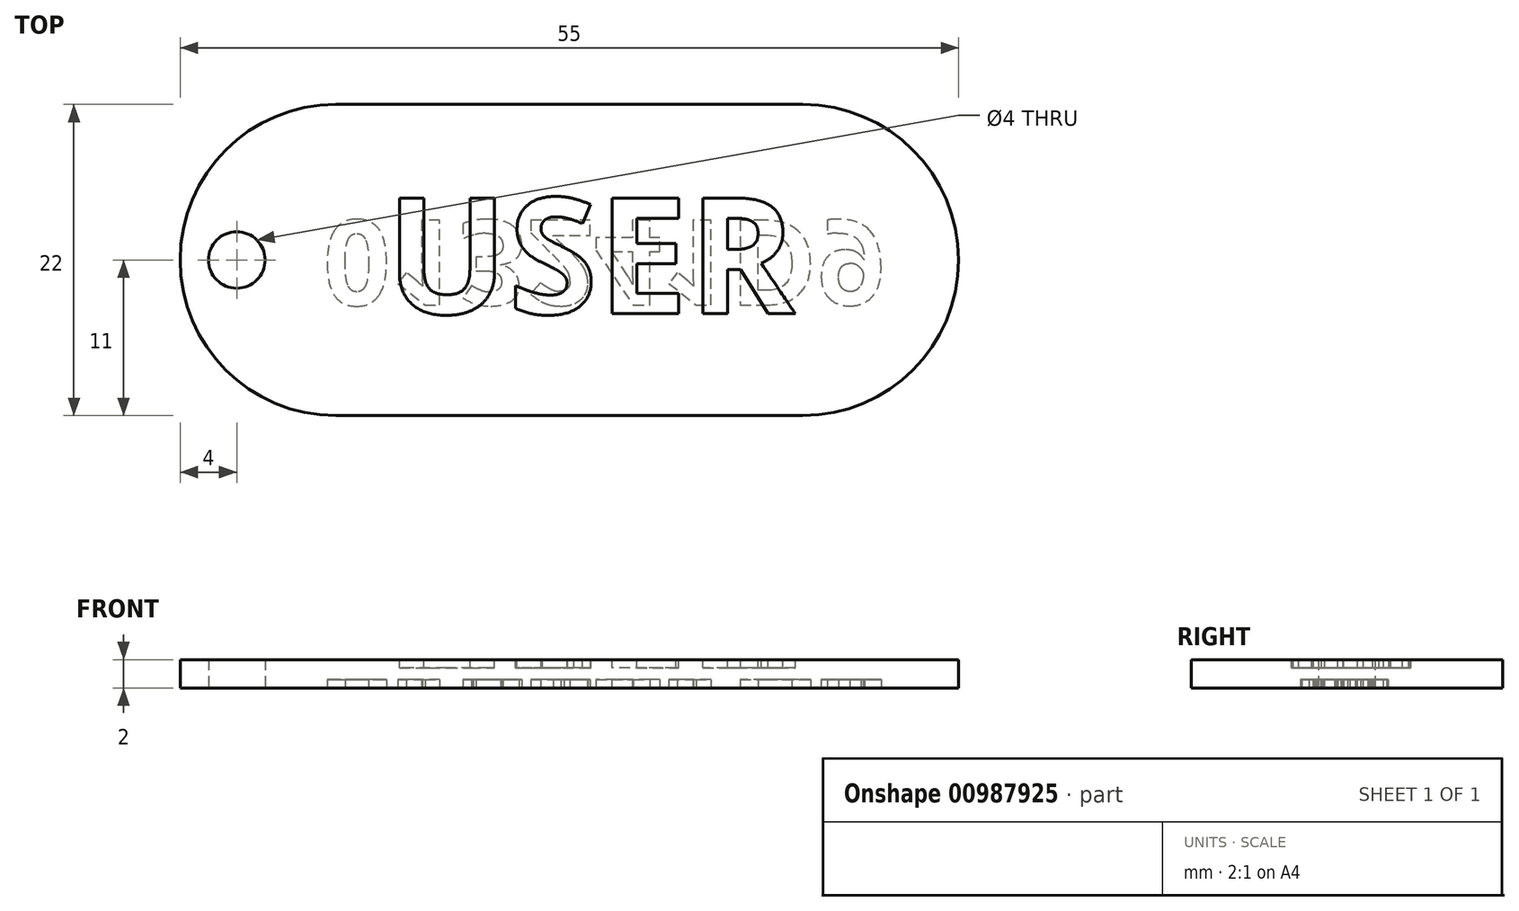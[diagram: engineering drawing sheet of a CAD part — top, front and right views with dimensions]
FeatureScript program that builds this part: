
annotation { "Feature Type Name" : "Feature", "Feature Type Description" : "" }
export const myFeature = defineFeature(function(context is Context, id is Id, definition is map)
    precondition{}
    {
        {
            var Q0;
            Q0=qCreatedBy(makeId("Top.planeOp"),FACE);
            var sketch = newSketch(context, id + "F0", { "sketchPlane" : qUnion([Q0])});
            skLineSegment(sketch, "E0.bottom", {"start": v(16.5, -11) * mm, "end": v(-16.5, -11) * mm});
            skLineSegment(sketch, "E0.top", {"start": v(16.5, 11) * mm, "end": v(-16.5, 11) * mm});
            skLineSegment(sketch, "E0.left", {"start": v(16.5, -11) * mm, "end": v(16.5, 11) * mm});
            skLineSegment(sketch, "E0.right", {"start": v(-16.5, -11) * mm, "end": v(-16.5, 11) * mm});
            skPoint(sketch, "E0.middle", {"position": v(0, 0) * mm});
            skCircle(sketch, "E1", {"center": v(-16.5, 0) * mm, "radius": 11 * mm});
            skCircle(sketch, "E2", {"center": v(16.5, 0) * mm, "radius": 11 * mm});
            skPoint(sketch, "E3", {"position": v(-23.5, 0) * mm});
            skSolve(sketch);
        }
        {
            var Q0;
            {var subQ0=sQuery(id+"F0.wireOp",EDGE,"E0.right");Q0=makeQuery(id+"F0.imprint","IMPRINT",FACE,{"disambiguationData":[TD([[makeQuery(id+"F0.imprint","IMPRINT",EDGE,{"derivedFrom":subQ0}),-1.0]])]});}
            var Q1;
            {var subQ0=sQuery(id+"F0.wireOp",EDGE,"E0.right");Q1=makeQuery(id+"F0.imprint","IMPRINT",FACE,{"disambiguationData":[TD([[makeQuery(id+"F0.imprint","IMPRINT",EDGE,{"derivedFrom":subQ0}),1.0]])]});}
            var Q2;
            {var subQ0=sQuery(id+"F0.wireOp",EDGE,"E0.left");Q2=makeQuery(id+"F0.imprint","IMPRINT",FACE,{"disambiguationData":[TD([[makeQuery(id+"F0.imprint","IMPRINT",EDGE,{"derivedFrom":subQ0}),1.0]])]});}
            var Q3;
            {var subQ0=sQuery(id+"F0.wireOp",EDGE,"E0.bottom");Q3=makeQuery(id+"F0.imprint","IMPRINT",FACE,{"disambiguationData":[TD([[makeQuery(id+"F0.imprint","IMPRINT",EDGE,{"derivedFrom":subQ0}),-1.0]])]});}
            var Q4;
            {var subQ0=sQuery(id+"F0.wireOp",EDGE,"E0.left");Q4=makeQuery(id+"F0.imprint","IMPRINT",FACE,{"disambiguationData":[TD([[makeQuery(id+"F0.imprint","IMPRINT",EDGE,{"derivedFrom":subQ0}),-1.0]])]});}
            extrude(context, id + "F1", {"entities" : qUnion([Q0, Q1, Q2, Q3, Q4]), "depth" : 2 * mm, "offsetDistance" : 25 * mm});
        }
        {
            var Q0;
            Q0=sQuery(id+"F0.wireOp",VERTEX,"E3");
            var Q1;
            Q1=makeQuery(id+"F1.opExtrude","SWEPT_BODY",BODY,{"disambiguationData":[OSD([sQuery(id+"F0.wireOp",EDGE,"E0.bottom"),sQuery(id+"F0.wireOp",EDGE,"E0.top"),sQuery(id+"F0.wireOp",EDGE,"E1"),sQuery(id+"F0.wireOp",EDGE,"E2")])]});
            hole(context, id + "F2", {"style" : HoleStyle.SIMPLE, "endStyle" : HoleEndStyle.THROUGH, "oppositeDirection" : true, "holeDiameter" : 4 * mm, "majorDiameter" : 5 * mm, "isTappedThrough" : true, "tappedDepth" : 12 * mm, "tapClearance" : 3, "locations" : qUnion([Q0]), "scope" : qUnion([Q1])});
        }
        {
            var Q0;
            Q0=makeQuery(id+"F1.opExtrude","CAP_FACE",FACE,{"disambiguationData":[OSD([sQuery(id+"F0.wireOp",EDGE,"E0.bottom"),sQuery(id+"F0.wireOp",EDGE,"E0.top"),sQuery(id+"F0.wireOp",EDGE,"E1"),sQuery(id+"F0.wireOp",EDGE,"E2")])],"isStart":false});
            var sketch = newSketch(context, id + "F3", { "sketchPlane" : qUnion([Q0])});
            skText(sketch, "E4", { "text": "USER", "fontName": "OpenSans-Bold.ttf"});
            const initialGuessF3  = {"E4": [-0.01298, -0.0038, 1, 0, 0.00825]};
            skSetInitialGuess(sketch, initialGuessF3);
            skSolve(sketch);
        }
        {
            var Q0;
            Q0=qSketchRegion(id+"F3",true);
            extrude(context, id + "F4", {"entities" : qUnion([Q0]), "operationType" : NewBodyOperationType.REMOVE, "oppositeDirection" : true, "depth" : 0.6 * mm, "offsetDistance" : 25 * mm});
        }
        {
            var Q0;
            Q0=makeQuery(id+"F1.opExtrude","CAP_FACE",FACE,{"disambiguationData":[OSD([sQuery(id+"F0.wireOp",EDGE,"E0.bottom"),sQuery(id+"F0.wireOp",EDGE,"E0.top"),sQuery(id+"F0.wireOp",EDGE,"E1"),sQuery(id+"F0.wireOp",EDGE,"E2")])],"isStart":true});
            var sketch = newSketch(context, id + "F5", { "sketchPlane" : qUnion([Q0])});
            skText(sketch, "E5", { "text": "013241D9", "fontName": "OpenSans-Bold.ttf"});
            const initialGuessF5  = {"E5": [-0.01741, -0.00281, 1, 0, 0.00604]};
            skSetInitialGuess(sketch, initialGuessF5);
            skSolve(sketch);
        }
        {
            var Q0;
            Q0=qSketchRegion(id+"F5",true);
            extrude(context, id + "F6", {"entities" : qUnion([Q0]), "operationType" : NewBodyOperationType.REMOVE, "oppositeDirection" : true, "depth" : 0.6 * mm, "offsetDistance" : 25 * mm});
        }
    });
